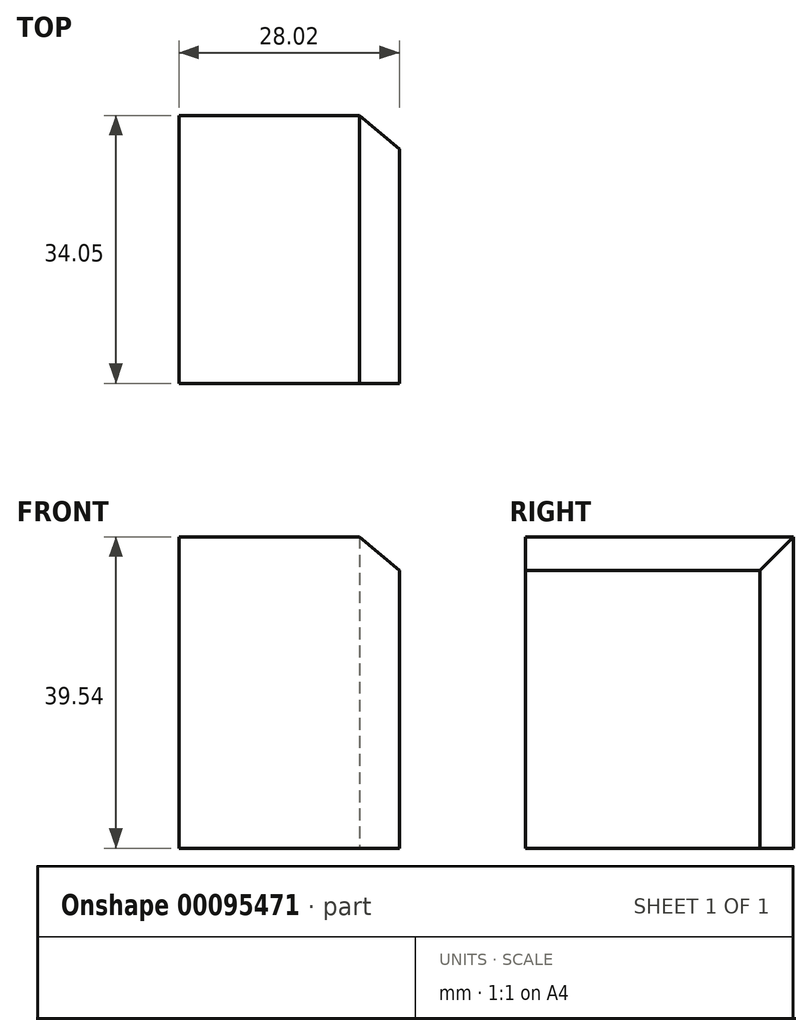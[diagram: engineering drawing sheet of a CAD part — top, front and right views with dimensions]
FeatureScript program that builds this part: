
annotation { "Feature Type Name" : "Feature", "Feature Type Description" : "" }
export const myFeature = defineFeature(function(context is Context, id is Id, definition is map)
    precondition{}
    {
        {
            var Q0;
            Q0=qCreatedBy(makeId("Top.planeOp"),FACE);
            var sketch = newSketch(context, id + "F0", { "sketchPlane" : qUnion([Q0])});
            skLineSegment(sketch, "E0.bottom", {"start": v(28.02, 34.05) * mm, "end": v(0, 34.05) * mm});
            skLineSegment(sketch, "E0.top", {"start": v(28.02, 0) * mm, "end": v(0, 0) * mm});
            skLineSegment(sketch, "E0.left", {"start": v(28.02, 34.05) * mm, "end": v(28.02, 0) * mm});
            skLineSegment(sketch, "E0.right", {"start": v(0, 34.05) * mm, "end": v(0, 0) * mm});
            skSolve(sketch);
        }
        {
            var Q0;
            Q0=makeQuery(id+"F0.imprint","IMPRINT",FACE,{"disambiguationData":[TD([[makeQuery(id+"F0.imprint","IMPRINT",EDGE,{"derivedFrom":sQuery(id+"F0.wireOp",EDGE,"E0.bottom")}),1.0]])]});
            extrude(context, id + "F1", {"entities" : qUnion([Q0]), "depth" : 39.54 * mm});
        }
        {
            var Q0;
            Q0=makeQuery(id+"F1.opExtrude","SWEPT_EDGE",EDGE,{"disambiguationData":[OSD([sQuery(id+"F0.wireOp",EDGE,"E0.bottom"),sQuery(id+"F0.wireOp",EDGE,"E0.left")])]});
            var Q1;
            Q1=makeQuery(id+"F1.opExtrude","CAP_EDGE",EDGE,{"disambiguationData":[OSD([sQuery(id+"F0.wireOp",EDGE,"E0.left")])],"isStart":false});
            chamfer(context, id + "F2", {"entities" : qUnion([Q0, Q1]), "chamferType" : ChamferType.OFFSET_ANGLE, "width" : 5.08 * mm, "oppositeDirection" : false, "angle" : 40 * degree, "tangentPropagation" : true});
        }
    });
